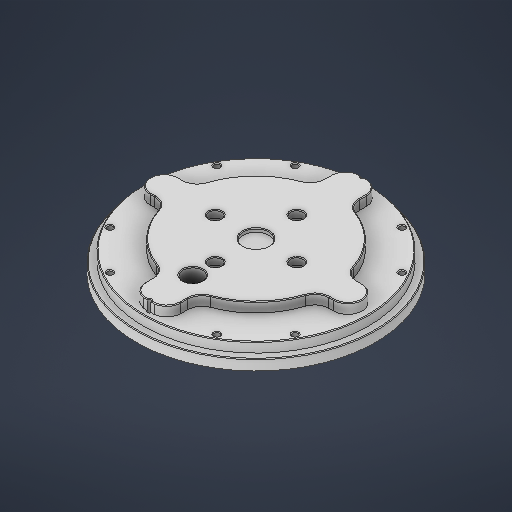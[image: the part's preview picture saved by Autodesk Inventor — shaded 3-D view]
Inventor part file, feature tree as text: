
AUTODESK INVENTOR PART (.ipt)
format: ipt  version: 2025 (Build 290162000, 162)  size: 510,464 bytes
history: native  units: in
note: dims shown in document units (in); Inventor stores cm internally (conversion verified against a paired STEP export)
features: sketch x13, extrude x8, hole x4, chamfer x4
ambient origin geometry x8: Origin, YZ Plane, XZ Plane, XY Plane, X Axis, Y Axis, Z Axis, Center Point
bodies: Solid1 (feature_tree)
feature tree (29):
  sketch  "Sketch1"  dims[d3=4.3307in d24=6.6929in]
  extrude  "Extrusion1"  Depth=6.6929in
  extrude  "Extrusion2"  Depth=5.9843in
  extrude  "Extrusion3"  Depth=4.3307in
  sketch  "Sketch2"  dims[d27=0.9843in d28=4.3307in]
  extrude  "Extrusion4"  Depth=0.3937in
  hole  "Hole1"  [1 undecoded]
  hole  "Hole2"  [1 undecoded]
  sketch  "Sketch4"  dims[d38=0.2953in d39=0.0in d40=2.2835in]
  extrude  "Extrusion5"  Depth=2.2835in
  extrude  "Extrusion6"  Depth=0.1969in
  hole  "Hole3"  [1 undecoded]
  chamfer  "Chamfer1"  Distance=0.7874in Angle=360.0deg
  chamfer  "Chamfer2"  Distance=3.1496in
  hole  "Hole5"  [1 undecoded]
  extrude  "Extrusion9"  Depth=0.3937in
  chamfer  "Chamfer3"  Distance=0.0591in
  extrude  "Extrusion10"  Depth=0.3937in TaperAngle=0.0deg
  chamfer  "Chamfer4"  Distance=0.1969in
  sketch  "Sketch Circular Pattern1"  dims[d25=6.2992in d26=5.9843in]
  sketch  "Sketch3"  dims[d31=0.3937in d32=0.3937in]
  sketch  "Sketch Circular Pattern2"  dims[d29=0.7874in d30=0.3937in]
  sketch  "Sketch5"  dims[d41=0.3543in d42=0.1969in]
  sketch  "Sketch Circular Pattern3"  dims[d34=0.8465in d35=0.0in d36=0.5709in d37=0.0in]
  sketch  "Sketch7"  dims[d56=5.9843in]
  sketch  "Sketch Circular Pattern5"  dims[d43=1.5748in d45=360.0deg d47=0.1969in d48=0.0in]
  sketch  "Sketch9"  dims[d57=0.1378in d58=0.7874in d60=360.0deg]
  sketch  "Sketch Circular Pattern6"  dims[d49=0.2165in d50=0.7874in d51=0.1575in d52=0.0787in d53=90.0deg d54=0.315in d55=0.8108in]
  sketch  "Sketch10"  dims[d62=0.0968in d63=1.0487in d64=0.1575in d65=0.0787in d66=90.0deg d67=0.4646in d68=0.8108in d69=3.1496in d70=0.1969in d71=0.7874in d72=0.0591in d73=0.0in d74=0.4724in d75=0.0in d76=0.1969in d77=4.7244in d79=360.0deg d81=0.1628in d82=0.3937in d83=0.1575in d84=0.0787in d85=90.0deg d86=0.3937in d87=0.8108in d88=0.0197in d89=0.0787in d90=45.0deg d91=0.0197in d92=0.0787in d93=45.0deg d107=3.7402in d108=0.1969in d109=6.2992in d111=360.0deg d113=0.1969in d114=0.7874in d115=0.748in d116=0.3543in d117=90.0deg d118=0.7874in d119=0.8108in d139=0.7185in d140=3.1496in d141=0.7185in d142=3.1496in d144=360.0deg d146=0.0984in d147=0.0in d148=0.0197in d149=0.0787in d150=45.0deg d151=0.5512in d152=1.7717in d153=0.0in d154=0.0in d155=0.0197in d156=0.0787in d157=45.0deg d158=0.5512in d159=1.7717in d137=0.0197in d138=0.0344in]
note: 4 required parameter values undecoded (feature->parameter linkage not recoverable at this tier; creation-order binding heuristic only, values carry confidence <= 0.55)
